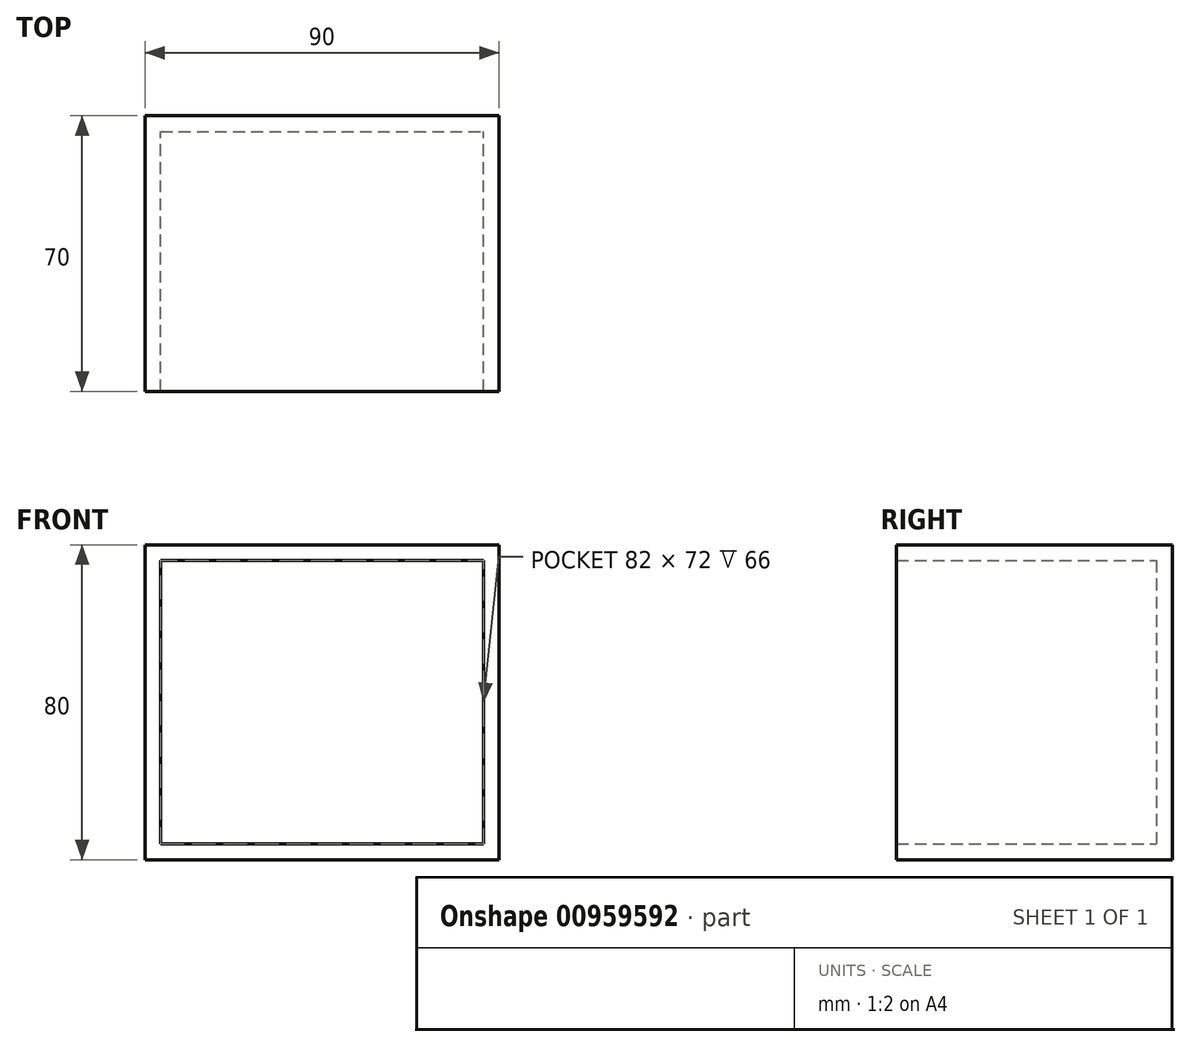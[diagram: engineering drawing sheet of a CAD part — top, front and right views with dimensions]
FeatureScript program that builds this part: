
annotation { "Feature Type Name" : "Feature", "Feature Type Description" : "" }
export const myFeature = defineFeature(function(context is Context, id is Id, definition is map)
    precondition{}
    {
        {
            var Q0;
            Q0=qCreatedBy(makeId("Front.planeOp"),FACE);
            var sketch = newSketch(context, id + "F0", { "sketchPlane" : qUnion([Q0])});
            skLineSegment(sketch, "E0.bottom", {"start": v(-31.2, 50.43) * mm, "end": v(50.8, 50.43) * mm});
            skLineSegment(sketch, "E0.top", {"start": v(-31.2, -21.57) * mm, "end": v(50.8, -21.57) * mm});
            skLineSegment(sketch, "E0.left", {"start": v(-31.2, 50.43) * mm, "end": v(-31.2, -21.57) * mm});
            skLineSegment(sketch, "E0.right", {"start": v(50.8, 50.43) * mm, "end": v(50.8, -21.57) * mm});
            skLineSegment(sketch, "E1.0", {"start": v(-35.2, 54.43) * mm, "end": v(54.8, 54.43) * mm});
            skLineSegment(sketch, "E1.1", {"start": v(-35.2, 54.43) * mm, "end": v(-35.2, -25.57) * mm});
            skLineSegment(sketch, "E1.2", {"start": v(-35.2, -25.57) * mm, "end": v(54.8, -25.57) * mm});
            skLineSegment(sketch, "E1.3", {"start": v(54.8, 54.43) * mm, "end": v(54.8, -25.57) * mm});
            skSolve(sketch);
        }
        {
            var Q0;
            Q0 = qSketchRegion(id + "F0", true);
            extrude(context, id + "F1", {"entities" : qUnion([Q0]), "depth" : 70 * mm, "offsetDistance" : 25 * mm});
        }
        {
            var Q0;
            Q0=makeQuery(id+"F0.imprint","IMPRINT",FACE,{"disambiguationData":[TD([[makeQuery(id+"F0.imprint","IMPRINT",EDGE,{"derivedFrom":sQuery(id+"F0.wireOp",EDGE,"E0.bottom")}),-1.0]])]});
            extrude(context, id + "F2", {"entities" : qUnion([Q0]), "operationType" : NewBodyOperationType.ADD, "depth" : 4 * mm, "offsetDistance" : 25 * mm});
        }
    });
